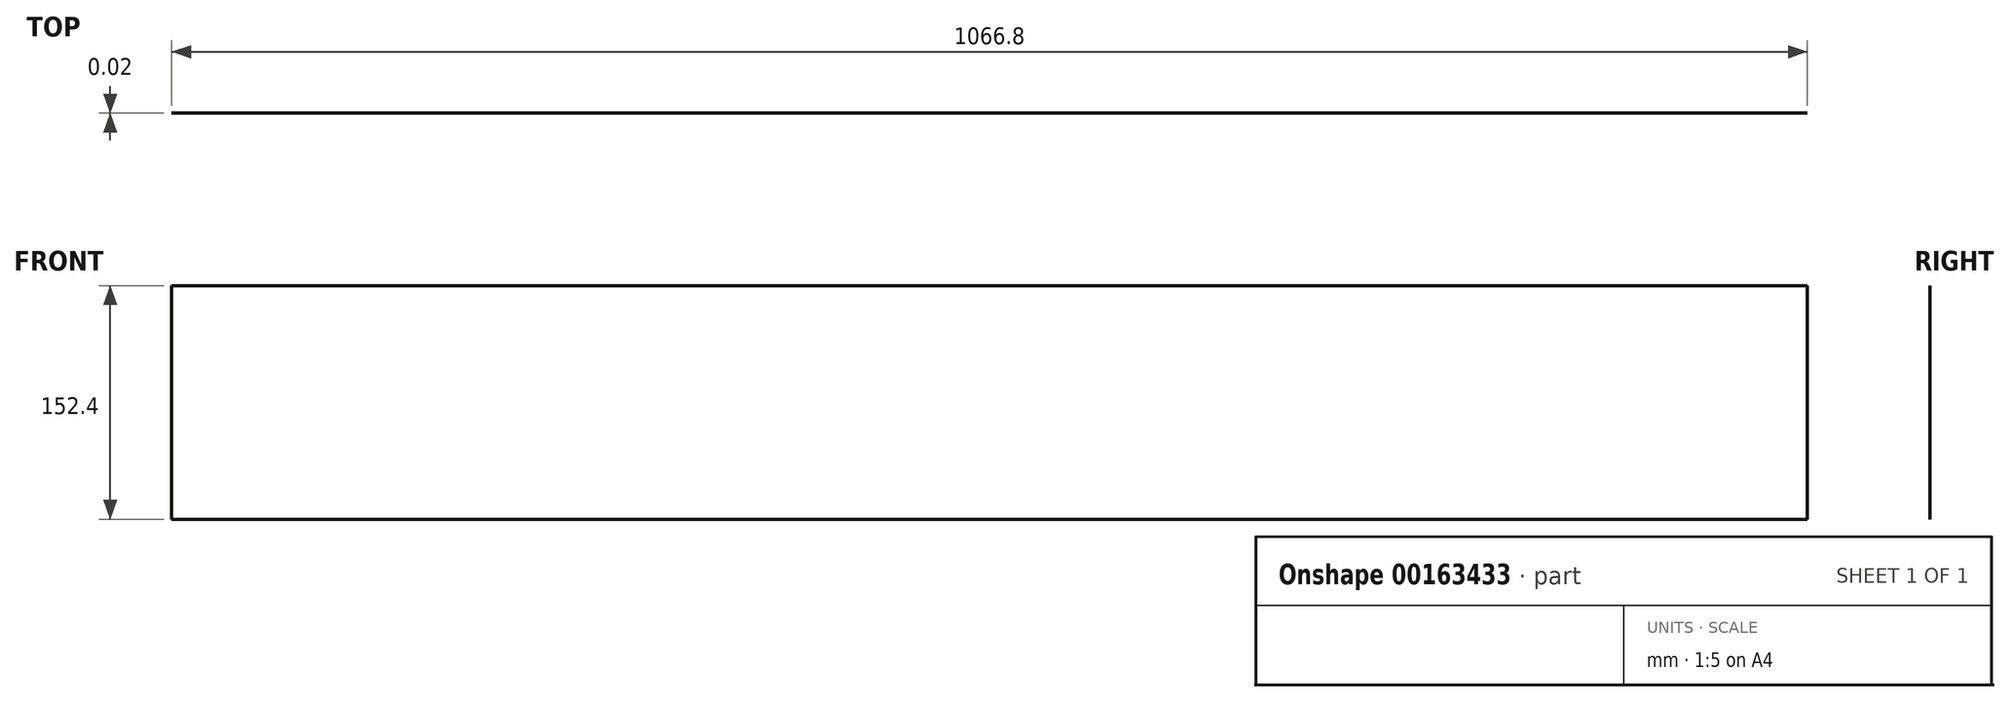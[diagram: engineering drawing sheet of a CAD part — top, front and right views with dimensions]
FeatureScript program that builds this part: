
annotation { "Feature Type Name" : "Feature", "Feature Type Description" : "" }
export const myFeature = defineFeature(function(context is Context, id is Id, definition is map)
    precondition{}
    {
        {
            var Q0;
            Q0=qCreatedBy(makeId("Front.planeOp"),FACE);
            var sketch = newSketch(context, id + "F0", { "sketchPlane" : qUnion([Q0])});
            skLineSegment(sketch, "E0.bottom", {"start": v(0, 0) * mm, "end": v(1066.8, 0) * mm});
            skLineSegment(sketch, "E0.top", {"start": v(0, 152.4) * mm, "end": v(1066.8, 152.4) * mm});
            skLineSegment(sketch, "E0.left", {"start": v(0, 0) * mm, "end": v(0, 152.4) * mm});
            skLineSegment(sketch, "E0.right", {"start": v(1066.8, 0) * mm, "end": v(1066.8, 152.4) * mm});
            skSolve(sketch);
        }
        {
            var Q0;
            Q0 = qSketchRegion(id + "F0", true);
            extrude(context, id + "F1", {"entities" : qUnion([Q0]), "depth" : 5 / 203.2 * mm});
        }
    });
